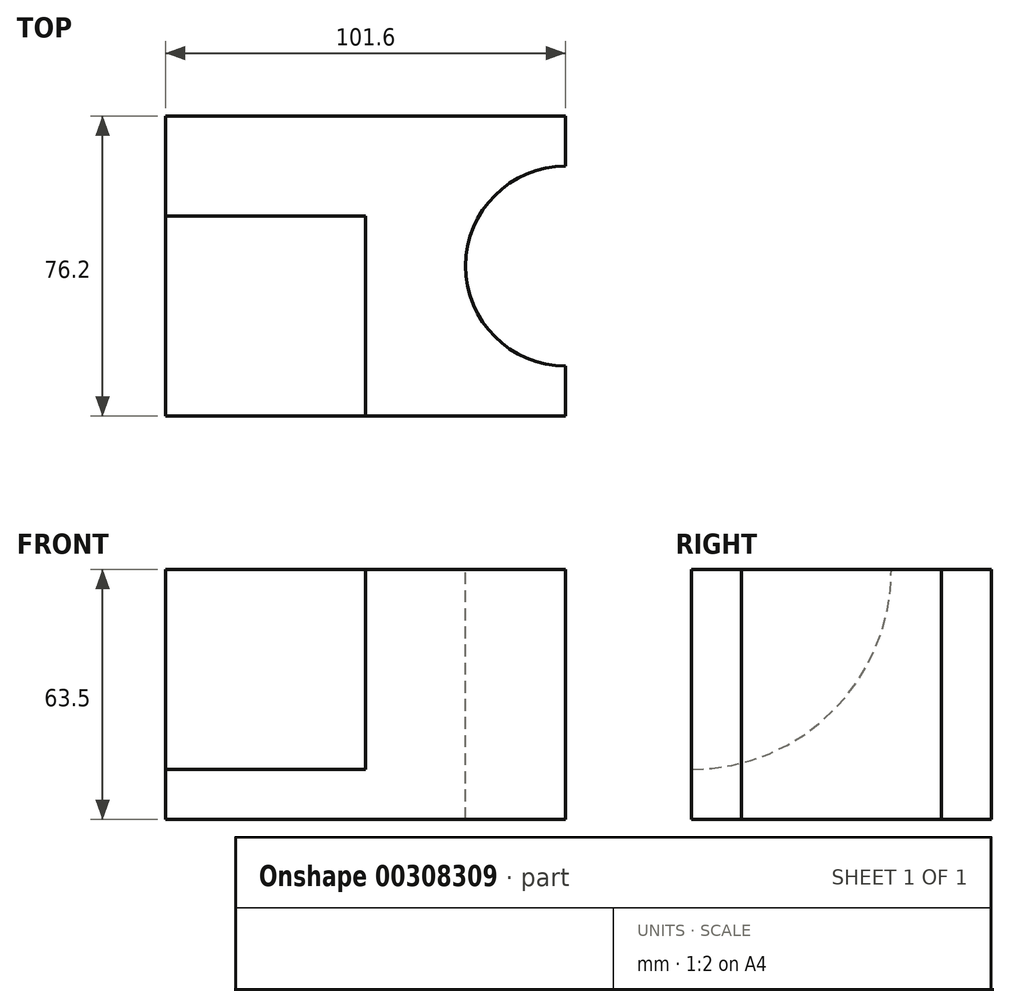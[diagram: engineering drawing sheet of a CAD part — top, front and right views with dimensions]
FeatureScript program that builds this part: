
annotation { "Feature Type Name" : "Feature", "Feature Type Description" : "" }
export const myFeature = defineFeature(function(context is Context, id is Id, definition is map)
    precondition{}
    {
        {
            var Q0;
            Q0=qCreatedBy(makeId("Front.planeOp"),FACE);
            var sketch = newSketch(context, id + "F0", { "sketchPlane" : qUnion([Q0])});
            skLineSegment(sketch, "E0", {"start": v(-54.06, -32.06) * mm, "end": v(47.54, -32.06) * mm});
            skLineSegment(sketch, "E1", {"start": v(-54.06, -32.06) * mm, "end": v(-54.06, 31.44) * mm});
            skLineSegment(sketch, "E2", {"start": v(-54.06, 31.44) * mm, "end": v(47.54, 31.44) * mm});
            skLineSegment(sketch, "E3", {"start": v(47.54, 31.44) * mm, "end": v(47.54, -32.06) * mm});
            skSolve(sketch);
        }
        {
            var Q0;
            Q0=makeQuery(id+"F0.imprint","IMPRINT",FACE,{"disambiguationData":[TD([[makeQuery(id+"F0.imprint","IMPRINT",EDGE,{"derivedFrom":sQuery(id+"F0.wireOp",EDGE,"E0")}),1.0]])]});
            extrude(context, id + "F1", {"entities" : qUnion([Q0]), "depth" : 76.2 * mm});
        }
        {
            var Q0;
            Q0=makeQuery(id+"F1.opExtrude","SWEPT_FACE",FACE,{"disambiguationData":[OSD([sQuery(id+"F0.wireOp",EDGE,"E2")])]});
            var sketch = newSketch(context, id + "F2", { "sketchPlane" : qUnion([Q0])});
            skArc(sketch, "E4", {"start": v(47.54, -12.7) * mm, "mid": v(22.14, -38.1) * mm, "end": v(47.54, -63.5) * mm});
            skLineSegment(sketch, "E5", {"start": v(0, 0) * mm, "end": v(47.54, 0) * mm});
            skLineSegment(sketch, "E6", {"start": v(47.54, 0) * mm, "end": v(47.54, -76.2) * mm});
            skSolve(sketch);
        }
        {
            var Q0;
            {var subQ0=sQuery(id+"F2.wireOp",EDGE,"E4");Q0=makeQuery(id+"F2.imprint","IMPRINT",FACE,{"disambiguationData":[TD([[makeQuery(id+"F2.imprint","IMPRINT",EDGE,{"derivedFrom":subQ0}),1.0]])]});}
            extrude(context, id + "F3", {"entities" : qUnion([Q0]), "operationType" : NewBodyOperationType.REMOVE, "oppositeDirection" : true, "depth" : 63.5 * mm});
        }
        {
            var Q0;
            Q0=makeQuery(id+"F1.opExtrude","SWEPT_FACE",FACE,{"disambiguationData":[OSD([sQuery(id+"F0.wireOp",EDGE,"E1")])]});
            var sketch = newSketch(context, id + "F4", { "sketchPlane" : qUnion([Q0])});
            skArc(sketch, "E7", {"start": v(25.4, 31.44) * mm, "mid": v(40.28, -4.48) * mm, "end": v(76.2, -19.36) * mm});
            skLineSegment(sketch, "E8", {"start": v(0, 31.44) * mm, "end": v(76.2, 31.44) * mm});
            skLineSegment(sketch, "E9", {"start": v(76.2, -34.61) * mm, "end": v(76.2, -32.06) * mm});
            skLineSegment(sketch, "E10", {"start": v(76.2, -32.06) * mm, "end": v(76.2, 31.44) * mm});
            skSolve(sketch);
        }
        {
            var Q0;
            {var subQ0=sQuery(id+"F4.wireOp",EDGE,"E7");Q0=makeQuery(id+"F4.imprint","IMPRINT",FACE,{"disambiguationData":[TD([[makeQuery(id+"F4.imprint","IMPRINT",EDGE,{"derivedFrom":subQ0}),1.0]])]});}
            extrude(context, id + "F5", {"entities" : qUnion([Q0]), "operationType" : NewBodyOperationType.REMOVE, "oppositeDirection" : true, "depth" : 50.8 * mm});
        }
    });
